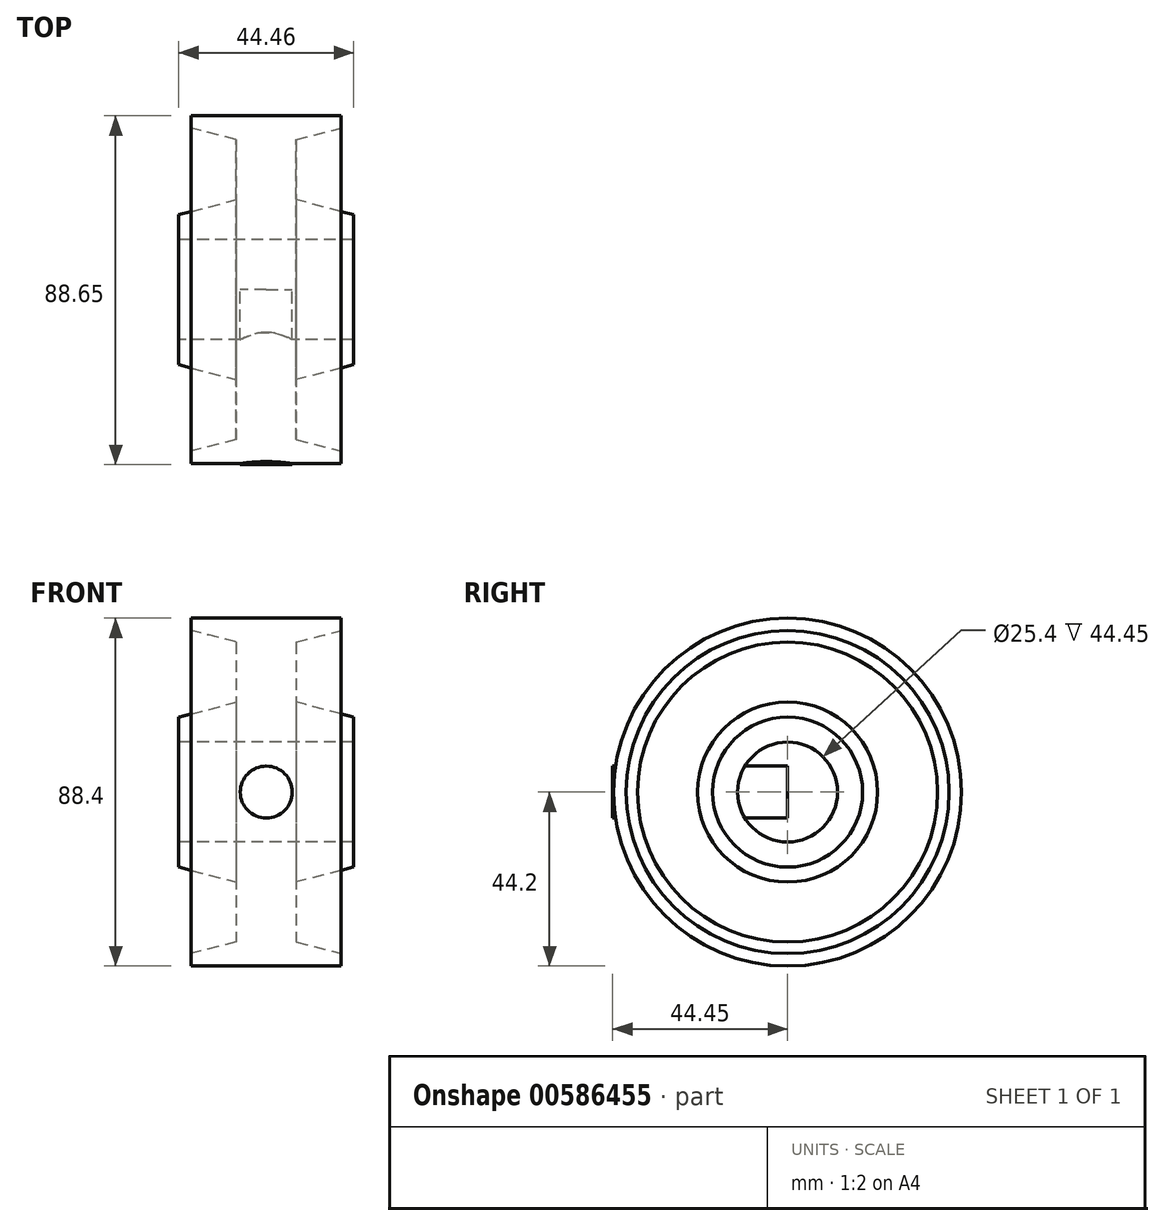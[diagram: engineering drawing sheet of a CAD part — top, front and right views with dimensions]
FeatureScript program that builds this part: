
annotation { "Feature Type Name" : "Feature", "Feature Type Description" : "" }
export const myFeature = defineFeature(function(context is Context, id is Id, definition is map)
    precondition{}
    {
        {
            var Q0;
            Q0=qCreatedBy(makeId("Front.planeOp"),FACE);
            var sketch = newSketch(context, id + "F0", { "sketchPlane" : qUnion([Q0])});
            skLineSegment(sketch, "E0", {"start": v(0, 12.7) * mm, "end": v(-22.22, 12.7) * mm});
            skLineSegment(sketch, "E1", {"start": v(-22.22, 12.7) * mm, "end": v(-22.22, 19.05) * mm});
            skLineSegment(sketch, "E2", {"start": v(-22.22, 19.05) * mm, "end": v(-7.62, 22.86) * mm});
            skLineSegment(sketch, "E3", {"start": v(-7.62, 22.86) * mm, "end": v(-7.62, 38.1) * mm});
            skLineSegment(sketch, "E4", {"start": v(-7.62, 38.1) * mm, "end": v(-19.05, 41.02) * mm});
            skLineSegment(sketch, "E5", {"start": v(-19.05, 41.02) * mm, "end": v(-19.05, 44.2) * mm});
            skLineSegment(sketch, "E6", {"start": v(-19.05, 44.2) * mm, "end": v(0, 44.2) * mm});
            skLineSegment(sketch, "E7", {"start": v(0, 44.2) * mm, "end": v(0, 12.7) * mm});
            skLineSegment(sketch, "E8", {"start": v(0, 12.7) * mm, "end": v(0, 0) * mm, "construction": true});
            skLineSegment(sketch, "E9", {"start": v(-13.92, 0) * mm, "end": v(10.85, 0) * mm, "construction": true});
            skSolve(sketch);
        }
        {
            var Q0;
            Q0 = qSketchRegion(id + "F0", true);
            var Q1;
            Q1=sQuery(id+"F0.wireOp",EDGE,"E9");
            revolve(context, id + "F1", {"entities" : qUnion([Q0]), "axis" : qUnion([Q1]), "revolveType" : RevolveType.FULL});
        }
        {
            var Q0;
            Q0=makeQuery(id+"F1.opRevolve","SWEPT_BODY",BODY,{"disambiguationData":[OSD([sQuery(id+"F0.wireOp",EDGE,"E0"),sQuery(id+"F0.wireOp",EDGE,"E1"),sQuery(id+"F0.wireOp",EDGE,"E2"),sQuery(id+"F0.wireOp",EDGE,"E3"),sQuery(id+"F0.wireOp",EDGE,"E4"),sQuery(id+"F0.wireOp",EDGE,"E5"),sQuery(id+"F0.wireOp",EDGE,"E6"),sQuery(id+"F0.wireOp",EDGE,"E7")])]});
            var Q1;
            Q1=makeQuery(id+"F1.opRevolve","SWEPT_FACE",FACE,{"disambiguationData":[OSD([sQuery(id+"F0.wireOp",EDGE,"E7")])]});
            mirror(context, id + "F2", {"operationType" : NewBodyOperationType.ADD, "entities" : qUnion([Q0]), "mirrorPlane" : qUnion([Q1])});
        }
        {
            var Q0;
            Q0=qCreatedBy(makeId("Front.planeOp"),FACE);
            var sketch = newSketch(context, id + "F3", { "sketchPlane" : qUnion([Q0])});
            skCircle(sketch, "E10", {"center": v(0, 0) * mm, "radius": 6.6 * mm});
            skSolve(sketch);
        }
        {
            var Q0;
            Q0=makeQuery(id+"F3.imprint","IMPRINT",FACE,{"disambiguationData":[TD([[makeQuery(id+"F3.imprint","IMPRINT",EDGE,{"derivedFrom":sQuery(id+"F3.wireOp",EDGE,"E10")}),1.0]])]});
            extrude(context, id + "F4", {"entities" : qUnion([Q0]), "operationType" : NewBodyOperationType.ADD, "depth" : 44.45 * mm, "offsetDistance" : 25.4 * mm});
        }
    });
